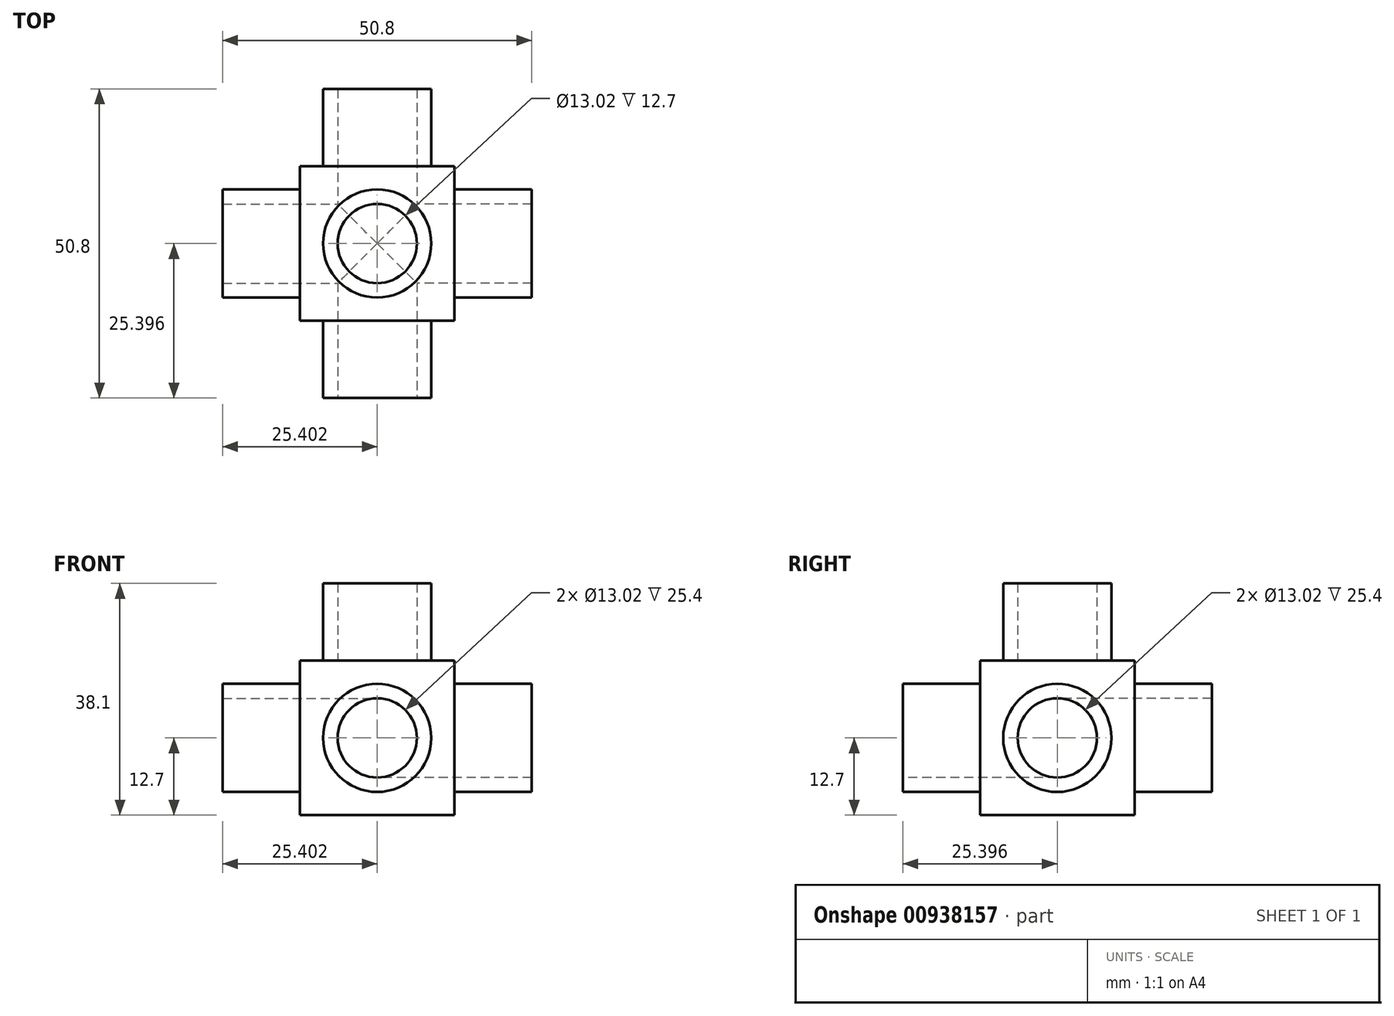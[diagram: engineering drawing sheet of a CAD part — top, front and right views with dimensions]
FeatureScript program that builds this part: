
annotation { "Feature Type Name" : "Feature", "Feature Type Description" : "" }
export const myFeature = defineFeature(function(context is Context, id is Id, definition is map)
    precondition{}
    {
        {
            var Q0;
            Q0=qCreatedBy(makeId("Top.planeOp"),FACE);
            var sketch = newSketch(context, id + "F0", { "sketchPlane" : qUnion([Q0])});
            skLineSegment(sketch, "E0.bottom", {"start": v(-30.77, 51) * mm, "end": v(-5.37, 51) * mm});
            skLineSegment(sketch, "E0.top", {"start": v(-30.77, 25.6) * mm, "end": v(-5.37, 25.6) * mm});
            skLineSegment(sketch, "E0.left", {"start": v(-30.77, 51) * mm, "end": v(-30.77, 25.6) * mm});
            skLineSegment(sketch, "E0.right", {"start": v(-5.37, 51) * mm, "end": v(-5.37, 25.6) * mm});
            skSolve(sketch);
        }
        {
            var Q0;
            Q0=makeQuery(id+"F0.imprint","IMPRINT",FACE,{"disambiguationData":[TD([[makeQuery(id+"F0.imprint","IMPRINT",EDGE,{"derivedFrom":sQuery(id+"F0.wireOp",EDGE,"E0.bottom")}),-1.0]])]});
            extrude(context, id + "F1", {"entities" : qUnion([Q0]), "depth" : 25.4 * mm, "offsetDistance" : 25 * mm});
        }
        {
            var Q0;
            Q0=makeQuery(id+"F1.opExtrude","CAP_FACE",FACE,{"disambiguationData":[OSD([sQuery(id+"F0.wireOp",EDGE,"E0.bottom"),sQuery(id+"F0.wireOp",EDGE,"E0.top"),sQuery(id+"F0.wireOp",EDGE,"E0.left"),sQuery(id+"F0.wireOp",EDGE,"E0.right")])],"isStart":false});
            var sketch = newSketch(context, id + "F2", { "sketchPlane" : qUnion([Q0])});
            skLineSegment(sketch, "E1", {"start": v(-5.37, 51) * mm, "end": v(-30.77, 25.6) * mm, "construction": true});
            skLineSegment(sketch, "E2", {"start": v(-5.37, 25.6) * mm, "end": v(-30.77, 51) * mm, "construction": true});
            skPoint(sketch, "E3", {"position": v(-18.07, 38.3) * mm});
            skCircle(sketch, "E4", {"center": v(-18.07, 38.3) * mm, "radius": 6.5 * mm});
            skCircle(sketch, "E5", {"center": v(-18.07, 38.3) * mm, "radius": 8.9 * mm});
            skSolve(sketch);
        }
        {
            var Q0;
            Q0 = qSketchRegion(id + "F2", true);
            extrude(context, id + "F3", {"entities" : qUnion([Q0]), "operationType" : NewBodyOperationType.ADD, "depth" : 12.7 * mm, "offsetDistance" : 25 * mm});
        }
        {
            var Q0;
            Q0=makeQuery(id+"F1.opExtrude","SWEPT_FACE",FACE,{"disambiguationData":[OSD([sQuery(id+"F0.wireOp",EDGE,"E0.bottom")])]});
            var sketch = newSketch(context, id + "F4", { "sketchPlane" : qUnion([Q0])});
            skLineSegment(sketch, "E6", {"start": v(30.77, 25.4) * mm, "end": v(5.37, 0) * mm, "construction": true});
            skLineSegment(sketch, "E7", {"start": v(30.77, 0) * mm, "end": v(5.37, 25.4) * mm, "construction": true});
            skPoint(sketch, "E8", {"position": v(18.07, 12.7) * mm});
            skCircle(sketch, "E9", {"center": v(18.07, 12.7) * mm, "radius": 6.5 * mm});
            skCircle(sketch, "E10", {"center": v(18.07, 12.7) * mm, "radius": 8.9 * mm});
            skSolve(sketch);
        }
        {
            var Q0;
            Q0=makeQuery(id+"F1.opExtrude","SWEPT_FACE",FACE,{"disambiguationData":[OSD([sQuery(id+"F0.wireOp",EDGE,"E0.right")])]});
            var sketch = newSketch(context, id + "F5", { "sketchPlane" : qUnion([Q0])});
            skLineSegment(sketch, "E11", {"start": v(51, 25.4) * mm, "end": v(25.6, 0) * mm, "construction": true});
            skLineSegment(sketch, "E12", {"start": v(51, 0) * mm, "end": v(25.6, 25.4) * mm, "construction": true});
            skPoint(sketch, "E13", {"position": v(38.3, 12.7) * mm});
            skCircle(sketch, "E14", {"center": v(38.3, 12.7) * mm, "radius": 6.5 * mm});
            skCircle(sketch, "E15", {"center": v(38.3, 12.7) * mm, "radius": 8.9 * mm});
            skSolve(sketch);
        }
        {
            var Q0;
            Q0=makeQuery(id+"F1.opExtrude","SWEPT_FACE",FACE,{"disambiguationData":[OSD([sQuery(id+"F0.wireOp",EDGE,"E0.top")])]});
            var sketch = newSketch(context, id + "F6", { "sketchPlane" : qUnion([Q0])});
            skLineSegment(sketch, "E16", {"start": v(-5.37, 25.4) * mm, "end": v(-30.77, 0) * mm, "construction": true});
            skLineSegment(sketch, "E17", {"start": v(-5.37, 0) * mm, "end": v(-30.77, 25.4) * mm, "construction": true});
            skPoint(sketch, "E18", {"position": v(-18.07, 12.7) * mm});
            skCircle(sketch, "E19", {"center": v(-18.07, 12.7) * mm, "radius": 6.5 * mm});
            skCircle(sketch, "E20", {"center": v(-18.07, 12.7) * mm, "radius": 8.9 * mm});
            skSolve(sketch);
        }
        {
            var Q0;
            Q0=makeQuery(id+"F1.opExtrude","SWEPT_FACE",FACE,{"disambiguationData":[OSD([sQuery(id+"F0.wireOp",EDGE,"E0.left")])]});
            var sketch = newSketch(context, id + "F7", { "sketchPlane" : qUnion([Q0])});
            skLineSegment(sketch, "E21", {"start": v(-25.6, 25.4) * mm, "end": v(-51, 0) * mm, "construction": true});
            skLineSegment(sketch, "E22", {"start": v(-25.6, 0) * mm, "end": v(-51, 25.4) * mm, "construction": true});
            skPoint(sketch, "E23", {"position": v(-38.3, 12.7) * mm});
            skCircle(sketch, "E24", {"center": v(-38.3, 12.7) * mm, "radius": 6.5 * mm});
            skCircle(sketch, "E25", {"center": v(-38.3, 12.7) * mm, "radius": 8.9 * mm});
            skSolve(sketch);
        }
        {
            var Q0;
            Q0 = qSketchRegion(id + "F4", true);
            extrude(context, id + "F8", {"entities" : qUnion([Q0]), "operationType" : NewBodyOperationType.ADD, "depth" : 12.7 * mm, "offsetDistance" : 25 * mm});
        }
        {
            var Q0;
            Q0 = qSketchRegion(id + "F5", true);
            extrude(context, id + "F9", {"entities" : qUnion([Q0]), "operationType" : NewBodyOperationType.ADD, "depth" : 12.7 * mm, "offsetDistance" : 25 * mm});
        }
        {
            var Q0;
            Q0 = qSketchRegion(id + "F6", true);
            extrude(context, id + "F10", {"entities" : qUnion([Q0]), "operationType" : NewBodyOperationType.ADD, "depth" : 12.7 * mm, "offsetDistance" : 25 * mm});
        }
        {
            var Q0;
            Q0 = qSketchRegion(id + "F7", true);
            extrude(context, id + "F11", {"entities" : qUnion([Q0]), "operationType" : NewBodyOperationType.ADD, "depth" : 12.7 * mm, "offsetDistance" : 25 * mm});
        }
        {
            var Q0;
            Q0=makeQuery(id+"F8.boolean.opBoolean","SPLIT",FACE,{"disambiguationData":[TD([makeQuery(id+"F8.opExtrude","SWEPT_FACE",FACE,{"disambiguationData":[OSD([sQuery(id+"F4.wireOp",EDGE,"E9")])]})])],"derivedFrom":makeQuery(id+"F1.opExtrude","SWEPT_FACE",FACE,{"disambiguationData":[OSD([sQuery(id+"F0.wireOp",EDGE,"E0.bottom")])]})});
            extrude(context, id + "F12", {"entities" : qUnion([Q0]), "operationType" : NewBodyOperationType.REMOVE, "oppositeDirection" : true, "depth" : 49 * mm, "offsetDistance" : 25 * mm});
        }
        {
            var Q0;
            Q0=makeQuery(id+"F11.boolean.opBoolean","SPLIT",FACE,{"disambiguationData":[TD([makeQuery(id+"F11.opExtrude","SWEPT_FACE",FACE,{"disambiguationData":[OSD([sQuery(id+"F7.wireOp",EDGE,"E24")])]})])],"derivedFrom":makeQuery(id+"F1.opExtrude","SWEPT_FACE",FACE,{"disambiguationData":[OSD([sQuery(id+"F0.wireOp",EDGE,"E0.left")])]})});
            extrude(context, id + "F13", {"entities" : qUnion([Q0]), "operationType" : NewBodyOperationType.REMOVE, "oppositeDirection" : true, "depth" : 55.7 * mm, "offsetDistance" : 25 * mm});
        }
    });
